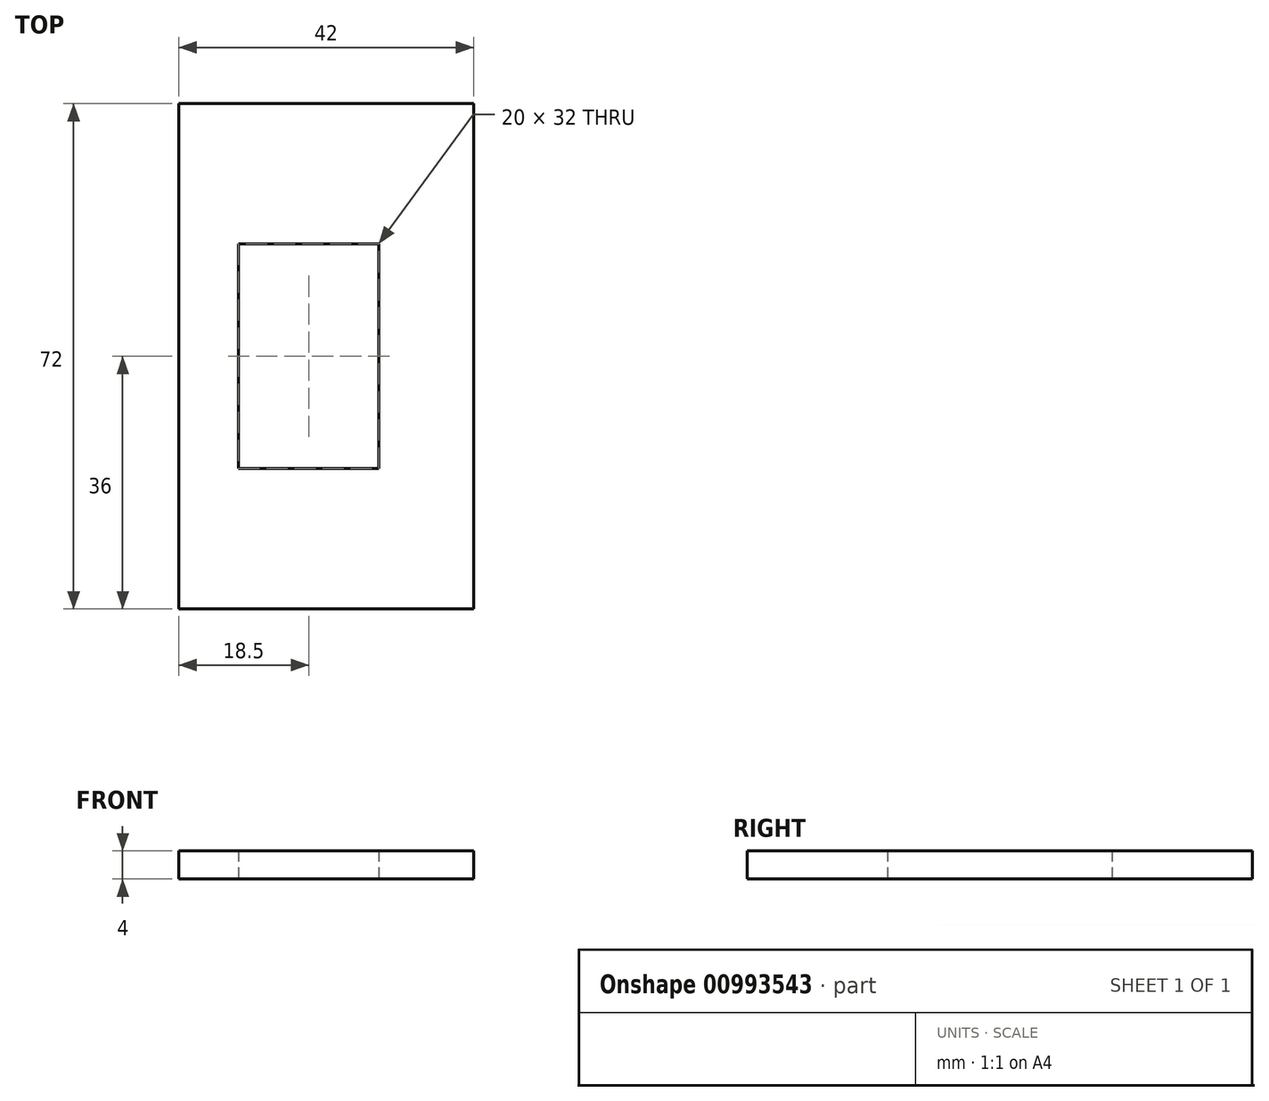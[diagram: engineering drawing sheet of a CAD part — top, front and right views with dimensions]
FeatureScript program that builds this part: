
annotation { "Feature Type Name" : "Feature", "Feature Type Description" : "" }
export const myFeature = defineFeature(function(context is Context, id is Id, definition is map)
    precondition{}
    {
        {
            var Q0;
            Q0=qCreatedBy(makeId("Top.planeOp"),FACE);
            var sketch = newSketch(context, id + "F0", { "sketchPlane" : qUnion([Q0])});
            skLineSegment(sketch, "E0", {"start": v(-12.5, 16) * mm, "end": v(7.5, 16) * mm});
            skLineSegment(sketch, "E1", {"start": v(-12.5, -16) * mm, "end": v(7.5, -16) * mm});
            skLineSegment(sketch, "E2", {"start": v(7.5, -16) * mm, "end": v(7.5, 16) * mm});
            skLineSegment(sketch, "E3", {"start": v(-12.5, -16) * mm, "end": v(-12.5, 16) * mm});
            skLineSegment(sketch, "E4", {"start": v(-21, 36) * mm, "end": v(-21, -36) * mm});
            skLineSegment(sketch, "E5", {"start": v(21, 36) * mm, "end": v(21, -36) * mm});
            skLineSegment(sketch, "E6", {"start": v(21, 36) * mm, "end": v(-21, 36) * mm});
            skLineSegment(sketch, "E7", {"start": v(21, -36) * mm, "end": v(-21, -36) * mm});
            skSolve(sketch);
        }
        {
            var Q0;
            Q0=makeQuery(id+"F0.imprint","IMPRINT",FACE,{"disambiguationData":[TD([[makeQuery(id+"F0.imprint","IMPRINT",EDGE,{"derivedFrom":sQuery(id+"F0.wireOp",EDGE,"E0")}),1.0]])]});
            extrude(context, id + "F1", {"entities" : qUnion([Q0]), "depth" : 4 * mm, "offsetDistance" : 25 * mm});
        }
    });
